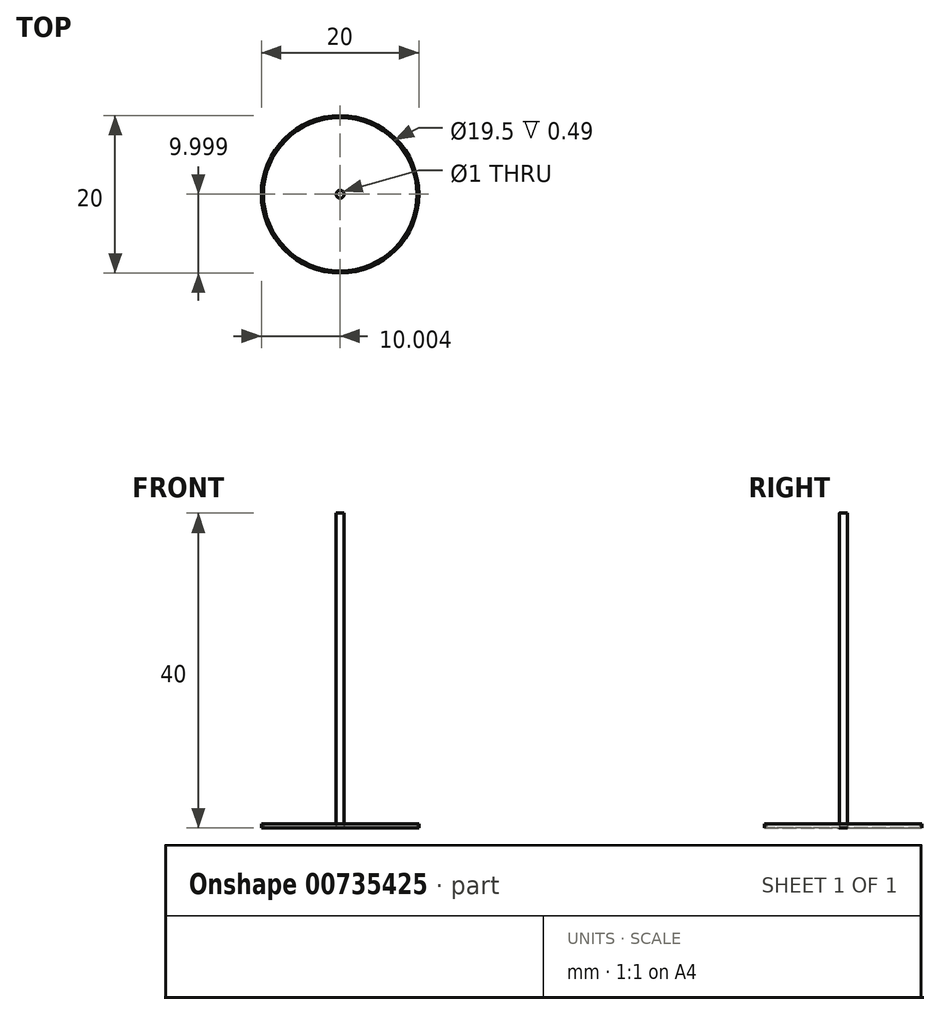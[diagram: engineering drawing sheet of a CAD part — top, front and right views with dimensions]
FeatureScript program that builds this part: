
annotation { "Feature Type Name" : "Feature", "Feature Type Description" : "" }
export const myFeature = defineFeature(function(context is Context, id is Id, definition is map)
    precondition{}
    {
        {
            var Q0;
            Q0=qCreatedBy(makeId("Top.planeOp"),FACE);
            var sketch = newSketch(context, id + "F0", { "sketchPlane" : qUnion([Q0])});
            skCircle(sketch, "E0", {"center": v(2, 6.38) * mm, "radius": 10 * mm});
            skCircle(sketch, "E1", {"center": v(2, 6.38) * mm, "radius": 0.5 * mm});
            skCircle(sketch, "E2", {"center": v(2, 6.38) * mm, "radius": 9.75 * mm});
            skSolve(sketch);
        }
        {
            var Q0;
            Q0=makeQuery(id+"F0.imprint","IMPRINT",FACE,{"disambiguationData":[TD([[makeQuery(id+"F0.imprint","IMPRINT",EDGE,{"derivedFrom":sQuery(id+"F0.wireOp",EDGE,"E1")}),1.0]])]});
            extrude(context, id + "F1", {"entities" : qUnion([Q0]), "depth" : 42.5 * mm, "offsetDistance" : 25 * mm});
        }
        {
            var Q0;
            Q0=makeQuery(id+"F0.imprint","IMPRINT",FACE,{"disambiguationData":[TD([[makeQuery(id+"F0.imprint","IMPRINT",EDGE,{"derivedFrom":sQuery(id+"F0.wireOp",EDGE,"E0")}),1.0]])]});
            extrude(context, id + "F2", {"entities" : qUnion([Q0]), "depth" : 0.5 * mm, "offsetDistance" : 25 * mm});
        }
        {
            var Q0;
            Q0=makeQuery(id+"F1.opExtrude","CAP_FACE",FACE,{"disambiguationData":[OSD([sQuery(id+"F0.wireOp",EDGE,"E1")])],"isStart":true});
            var sketch = newSketch(context, id + "F3", { "sketchPlane" : qUnion([Q0])});
            skCircle(sketch, "E3", {"center": v(2, -6.38) * mm, "radius": 10 * mm});
            skSolve(sketch);
        }
        {
            var Q0;
            Q0=makeQuery(id+"F3.imprint","IMPRINT",FACE,{"disambiguationData":[TD([[makeQuery(id+"F3.imprint","IMPRINT",EDGE,{"derivedFrom":sQuery(id+"F3.wireOp",EDGE,"E3")}),1.0]])]});
            extrude(context, id + "F4", {"entities" : qUnion([Q0]), "oppositeDirection" : true, "depth" : 0.5 * mm, "offsetDistance" : 25 * mm});
        }
        {
            var Q0;
            Q0=makeQuery(id+"F4.opExtrude","CAP_FACE",FACE,{"disambiguationData":[OSD([sQuery(id+"F0.wireOp",EDGE,"E1"),sQuery(id+"F3.wireOp",EDGE,"4dp0710i-FjK2-cs24-RJgh-WOHdKyYt1GAg")])],"isStart":true});
            extrude(context, id + "F5", {"entities" : qUnion([Q0]), "depth" : 0.05 * mm, "offsetDistance" : 25 * mm});
        }
        {
            var Q0;
            Q0=makeQuery(id+"F5.opExtrude","CAP_FACE",FACE,{"disambiguationData":[OSD([sQuery(id+"F0.wireOp",EDGE,"E1"),sQuery(id+"F3.wireOp",EDGE,"4dp0710i-FjK2-cs24-RJgh-WOHdKyYt1GAg")])],"isStart":false});
            extrude(context, id + "F6", {"entities" : qUnion([Q0]), "operationType" : NewBodyOperationType.REMOVE, "oppositeDirection" : true, "depth" : 0.06 * mm, "offsetDistance" : 25 * mm});
        }
        {
            var Q0;
            Q0=makeQuery(id+"F1.opExtrude","CAP_FACE",FACE,{"disambiguationData":[OSD([sQuery(id+"F0.wireOp",EDGE,"E1")])],"isStart":false});
            extrude(context, id + "F7", {"entities" : qUnion([Q0]), "operationType" : NewBodyOperationType.REMOVE, "oppositeDirection" : true, "depth" : 2.5 * mm, "offsetDistance" : 25 * mm});
        }
    });
